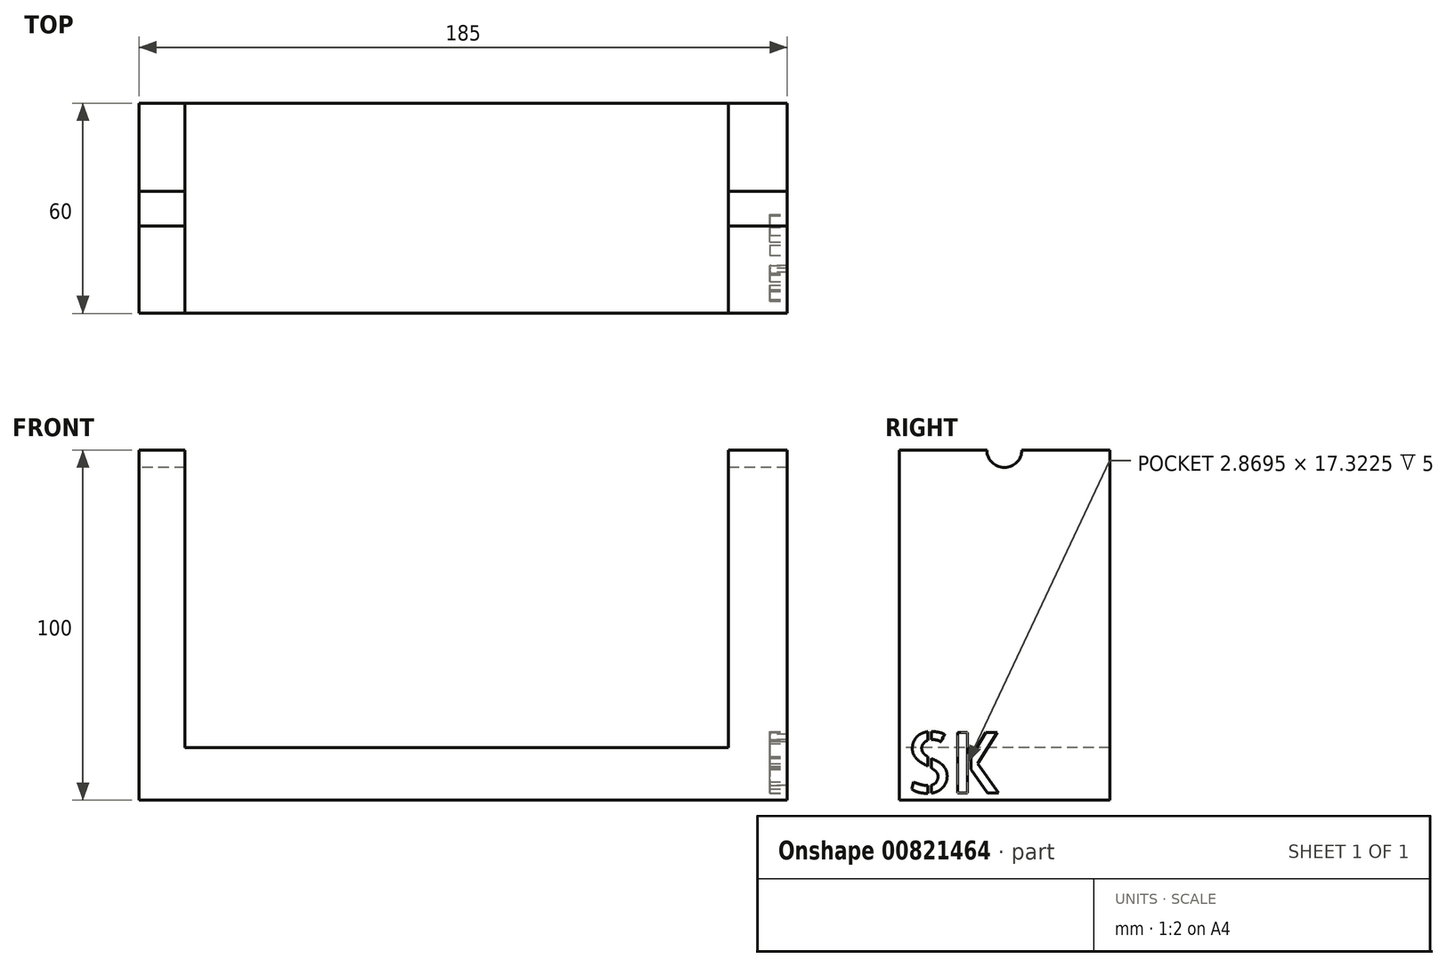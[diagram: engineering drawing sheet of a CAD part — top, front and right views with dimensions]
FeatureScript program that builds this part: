
annotation { "Feature Type Name" : "Feature", "Feature Type Description" : "" }
export const myFeature = defineFeature(function(context is Context, id is Id, definition is map)
    precondition{}
    {
        {
            var Q0;
            Q0=qCreatedBy(makeId("Top.planeOp"),FACE);
            var sketch = newSketch(context, id + "F0", { "sketchPlane" : qUnion([Q0])});
            skLineSegment(sketch, "E0.bottom", {"start": v(-89.77, 30.1) * mm, "end": v(95.23, 30.1) * mm});
            skLineSegment(sketch, "E0.top", {"start": v(-89.77, -29.9) * mm, "end": v(95.23, -29.9) * mm});
            skLineSegment(sketch, "E0.left", {"start": v(-89.77, 30.1) * mm, "end": v(-89.77, -29.9) * mm});
            skLineSegment(sketch, "E0.right", {"start": v(95.23, 30.1) * mm, "end": v(95.23, -29.9) * mm});
            skSolve(sketch);
        }
        {
            var Q0;
            Q0=makeQuery(id+"F0.imprint","IMPRINT",FACE,{"disambiguationData":[TD([[makeQuery(id+"F0.imprint","IMPRINT",EDGE,{"derivedFrom":sQuery(id+"F0.wireOp",EDGE,"E0.bottom")}),-1.0]])]});
            extrude(context, id + "F1", {"entities" : qUnion([Q0]), "depth" : 100 * mm, "offsetDistance" : 25.4 * mm});
        }
        {
            var Q0;
            Q0=makeQuery(id+"F1.opExtrude","SWEPT_FACE",FACE,{"disambiguationData":[OSD([sQuery(id+"F0.wireOp",EDGE,"E0.top")])]});
            var sketch = newSketch(context, id + "F2", { "sketchPlane" : qUnion([Q0])});
            skLineSegment(sketch, "E1.bottom", {"start": v(-76.64, 100) * mm, "end": v(78.36, 100) * mm});
            skLineSegment(sketch, "E1.top", {"start": v(-76.64, 15) * mm, "end": v(78.36, 15) * mm});
            skLineSegment(sketch, "E1.left", {"start": v(-76.64, 100) * mm, "end": v(-76.64, 15) * mm});
            skLineSegment(sketch, "E1.right", {"start": v(78.36, 100) * mm, "end": v(78.36, 15) * mm});
            skSolve(sketch);
        }
        {
            var Q0;
            Q0=makeQuery(id+"F2.imprint","IMPRINT",FACE,{"disambiguationData":[TD([[makeQuery(id+"F2.imprint","IMPRINT",EDGE,{"derivedFrom":sQuery(id+"F2.wireOp",EDGE,"E1.bottom")}),-1.0]])]});
            extrude(context, id + "F3", {"entities" : qUnion([Q0]), "operationType" : NewBodyOperationType.REMOVE, "endBound" : BoundingType.THROUGH_ALL, "oppositeDirection" : true, "depth" : 25.4 * mm, "offsetDistance" : 25.4 * mm});
        }
        {
            var Q0;
            Q0=makeQuery(id+"F1.opExtrude","SWEPT_FACE",FACE,{"disambiguationData":[OSD([sQuery(id+"F0.wireOp",EDGE,"E0.left")])]});
            var sketch = newSketch(context, id + "F4", { "sketchPlane" : qUnion([Q0])});
            skCircle(sketch, "E2", {"center": v(0, 100) * mm, "radius": 5 * mm});
            skSolve(sketch);
        }
        {
            var Q0;
            {var subQ0=sQuery(id+"F4.wireOp",EDGE,"E2");var subQ1=makeQuery(id+"F1.opExtrude","CAP_EDGE",EDGE,{"disambiguationData":[OSD([sQuery(id+"F0.wireOp",EDGE,"E0.left")])],"isStart":false});var subQ2=makeQuery(id+"F4.imprint","INTERSECT",VERTEX,{"disambiguationData":[OD(0.0)],"derivedFrom":[subQ1,subQ0]});Q0=makeQuery(id+"F4.imprint","IMPRINT",FACE,{"disambiguationData":[TD([[makeQuery(id+"F4.imprint","IMPRINT",EDGE,{"disambiguationData":[TD([[subQ2,-1.0]])],"derivedFrom":subQ0}),1.0]])]});}
            extrude(context, id + "F5", {"entities" : qUnion([Q0]), "operationType" : NewBodyOperationType.REMOVE, "endBound" : BoundingType.THROUGH_ALL, "oppositeDirection" : true, "depth" : 25.4 * mm, "offsetDistance" : 25.4 * mm});
        }
        {
            var Q0;
            Q0=makeQuery(id+"F1.opExtrude","SWEPT_FACE",FACE,{"disambiguationData":[OSD([sQuery(id+"F0.wireOp",EDGE,"E0.right")])]});
            var sketch = newSketch(context, id + "F6", { "sketchPlane" : qUnion([Q0])});
            skText(sketch, "E3", { "text": "SK", "fontName": "AllertaStencil-Regular.ttf"});
            const initialGuessF6  = {"E3": [-0.02827, 0.002, 1, 0, 0.01733]};
            skSetInitialGuess(sketch, initialGuessF6);
            skSolve(sketch);
        }
        {
            var Q0;
            Q0 = qSketchRegion(id + "F6", true);
            extrude(context, id + "F7", {"entities" : qUnion([Q0]), "operationType" : NewBodyOperationType.REMOVE, "oppositeDirection" : true, "depth" : 5 * mm, "offsetDistance" : 25.4 * mm});
        }
    });
